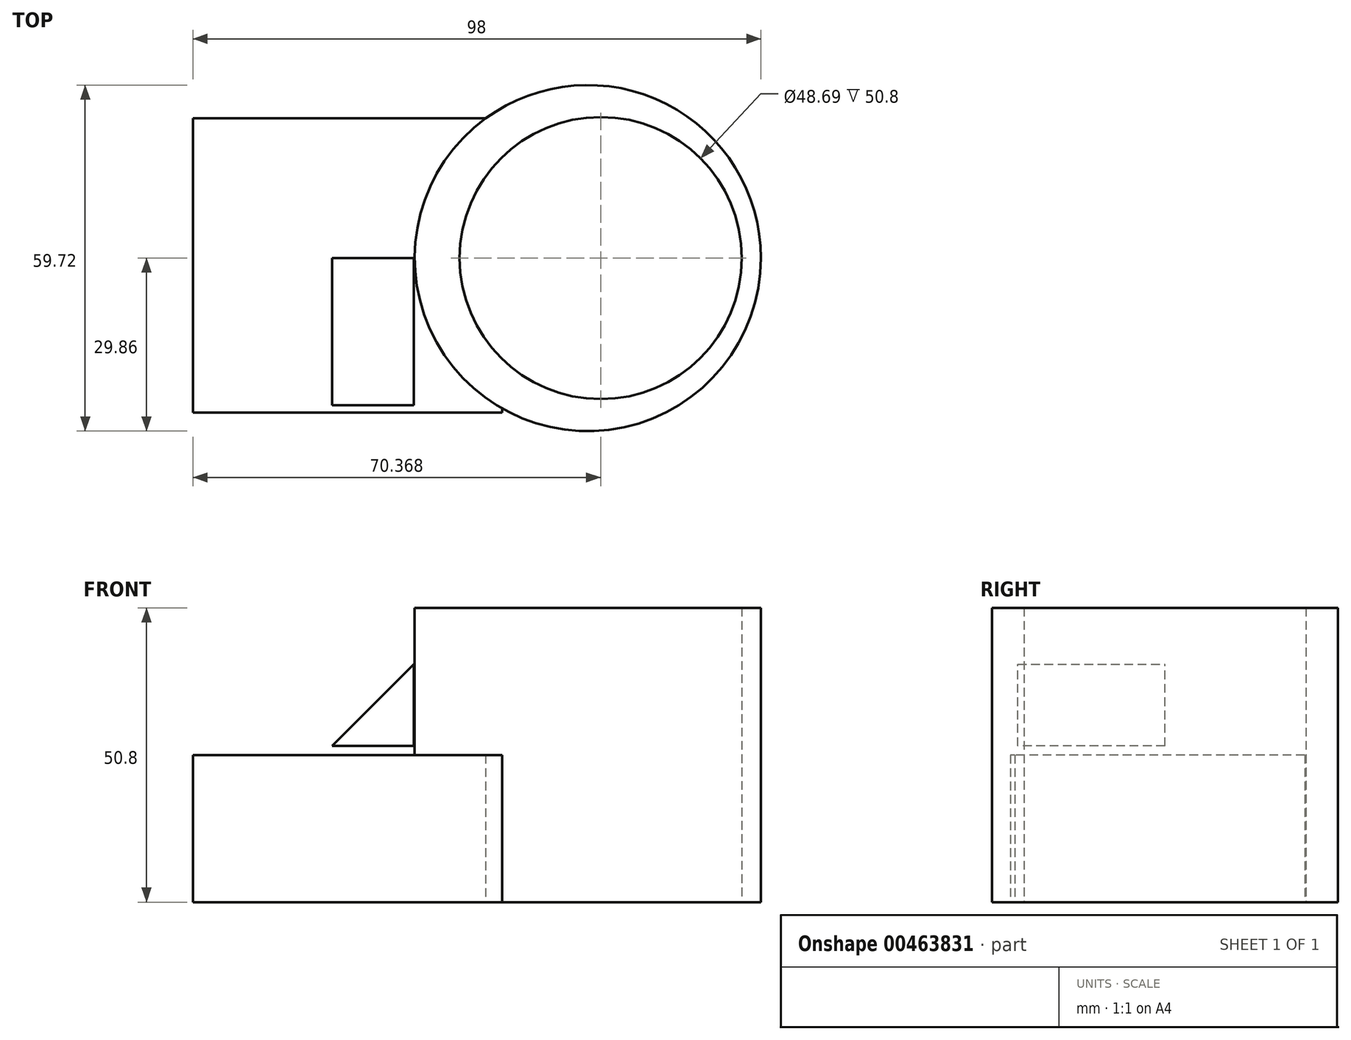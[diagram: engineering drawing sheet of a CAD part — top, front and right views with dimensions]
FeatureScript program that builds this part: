
annotation { "Feature Type Name" : "Feature", "Feature Type Description" : "" }
export const myFeature = defineFeature(function(context is Context, id is Id, definition is map)
    precondition{}
    {
        {
            var Q0;
            Q0=qCreatedBy(makeId("Top.planeOp"),FACE);
            var sketch = newSketch(context, id + "F0", { "sketchPlane" : qUnion([Q0])});
            skLineSegment(sketch, "E0.bottom", {"start": v(-38.15, 24.12) * mm, "end": v(15.19, 24.12) * mm});
            skLineSegment(sketch, "E0.top", {"start": v(-38.15, -26.67) * mm, "end": v(15.19, -26.67) * mm});
            skLineSegment(sketch, "E0.left", {"start": v(-38.15, 24.12) * mm, "end": v(-38.15, -26.67) * mm});
            skLineSegment(sketch, "E0.right", {"start": v(15.19, 24.12) * mm, "end": v(15.19, -26.67) * mm});
            skSolve(sketch);
        }
        {
            var Q0;
            Q0=qCreatedBy(makeId("Top.planeOp"),FACE);
            var sketch = newSketch(context, id + "F1", { "sketchPlane" : qUnion([Q0])});
            skCircle(sketch, "E1", {"center": v(29.99, 0) * mm, "radius": 29.86 * mm});
            skSolve(sketch);
        }
        {
            var Q0;
            Q0=makeQuery(id+"F1.imprint","IMPRINT",FACE,{"disambiguationData":[TD([[makeQuery(id+"F1.imprint","IMPRINT",EDGE,{"derivedFrom":sQuery(id+"F1.wireOp",EDGE,"E1")}),1.0]])]});
            extrude(context, id + "F2", {"entities" : qUnion([Q0]), "depth" : 50.8 * mm});
        }
        {
            var Q0;
            Q0=makeQuery(id+"F0.imprint","IMPRINT",FACE,{"disambiguationData":[TD([[makeQuery(id+"F0.imprint","IMPRINT",EDGE,{"derivedFrom":sQuery(id+"F0.wireOp",EDGE,"E0.bottom")}),-1.0]])]});
            extrude(context, id + "F3", {"entities" : qUnion([Q0]), "operationType" : NewBodyOperationType.ADD, "depth" : 25.4 * mm});
        }
        {
            var Q0;
            Q0=qCreatedBy(makeId("Top.planeOp"),FACE);
            var sketch = newSketch(context, id + "F4", { "sketchPlane" : qUnion([Q0])});
            skCircle(sketch, "E2", {"center": v(32.22, 0) * mm, "radius": 24.35 * mm});
            skSolve(sketch);
        }
        {
            var Q0;
            Q0=makeQuery(id+"F4.imprint","IMPRINT",FACE,{"disambiguationData":[TD([[makeQuery(id+"F4.imprint","IMPRINT",EDGE,{"derivedFrom":sQuery(id+"F4.wireOp",EDGE,"E2")}),1.0]])]});
            extrude(context, id + "F5", {"entities" : qUnion([Q0]), "operationType" : NewBodyOperationType.REMOVE, "depth" : 63.5 * mm});
        }
        {
            var Q0;
            Q0=qCreatedBy(makeId("Front.planeOp"),FACE);
            var sketch = newSketch(context, id + "F6", { "sketchPlane" : qUnion([Q0])});
            skLineSegment(sketch, "E3.bottom", {"start": v(-24.03, 26.95) * mm, "end": v(0, 26.95) * mm});
            skLineSegment(sketch, "E3.top", {"start": v(-24.03, 42.44) * mm, "end": v(0, 42.44) * mm});
            skLineSegment(sketch, "E3.left", {"start": v(-24.03, 26.95) * mm, "end": v(-24.03, 42.44) * mm});
            skLineSegment(sketch, "E3.right", {"start": v(0, 26.95) * mm, "end": v(0, 42.44) * mm});
            skSolve(sketch);
        }
        {
            var Q0;
            Q0=makeQuery(id+"F6.imprint","IMPRINT",FACE,{"disambiguationData":[TD([[makeQuery(id+"F6.imprint","IMPRINT",EDGE,{"derivedFrom":sQuery(id+"F6.wireOp",EDGE,"E3.bottom")}),1.0]])]});
            extrude(context, id + "F7", {"entities" : qUnion([Q0]), "depth" : 25.4 * mm});
        }
        {
            var Q0;
            Q0=makeQuery(id+"F7.opExtrude","SWEPT_EDGE",EDGE,{"disambiguationData":[OSD([sQuery(id+"F6.wireOp",EDGE,"E3.top"),sQuery(id+"F6.wireOp",EDGE,"E3.left")])]});
            chamfer(context, id + "F8", {"entities" : qUnion([Q0]), "width" : 25.4 * mm, "tangentPropagation" : true});
        }
    });
